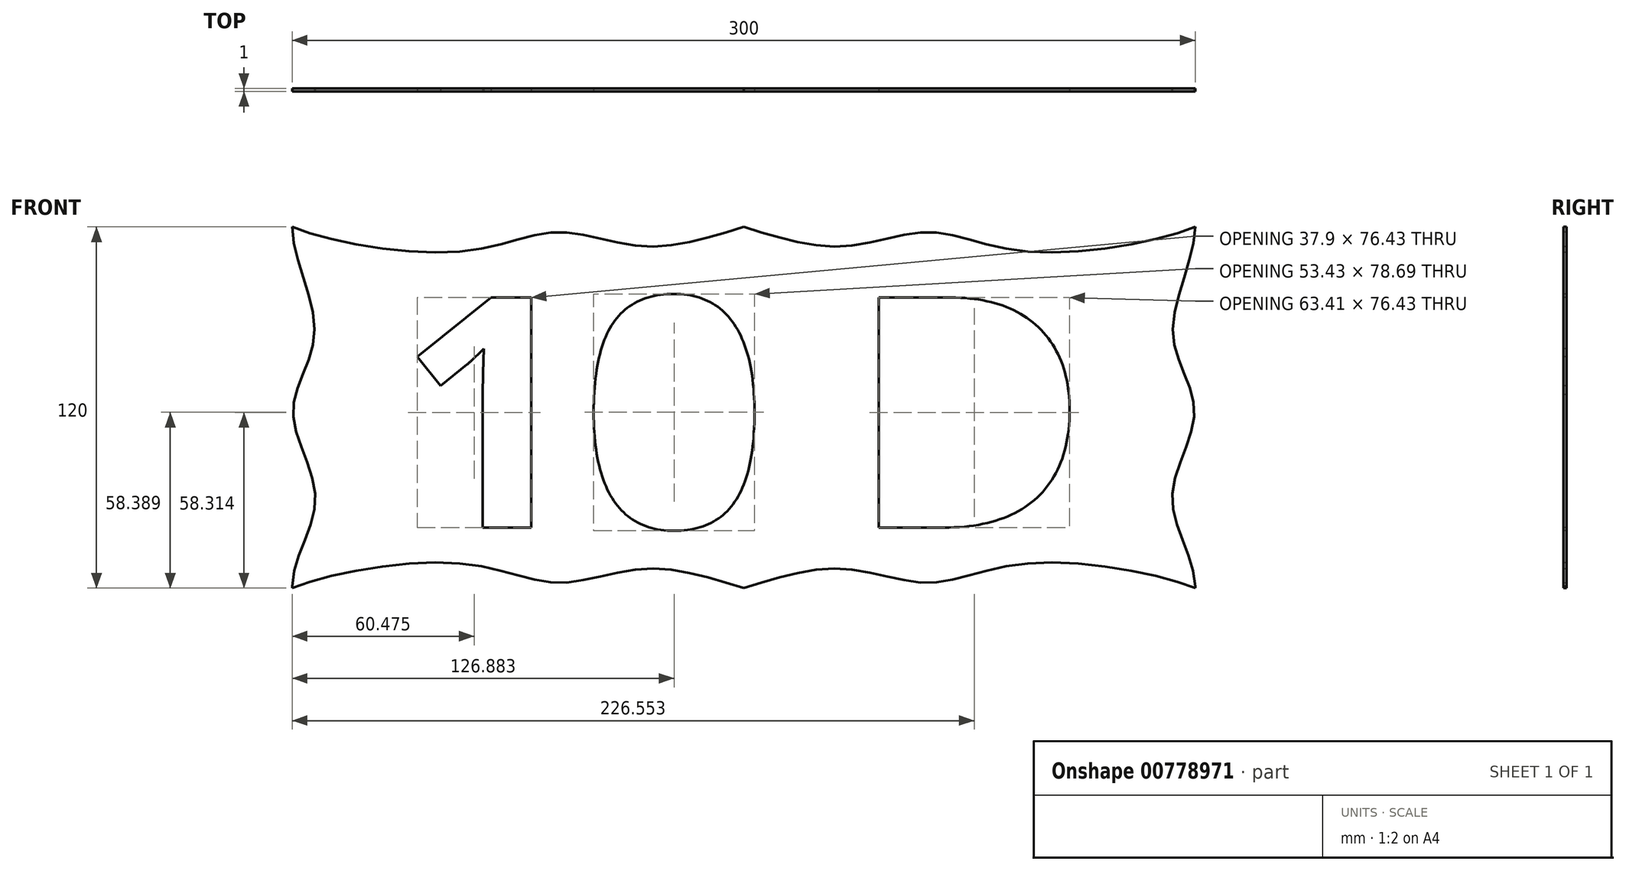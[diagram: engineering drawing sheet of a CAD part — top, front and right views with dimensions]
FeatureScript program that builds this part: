
annotation { "Feature Type Name" : "Feature", "Feature Type Description" : "" }
export const myFeature = defineFeature(function(context is Context, id is Id, definition is map)
    precondition{}
    {
        {
            var Q0;
            Q0=qCreatedBy(makeId("Front.planeOp"),FACE);
            var sketch = newSketch(context, id + "F0", { "sketchPlane" : qUnion([Q0])});
            skLineSegment(sketch, "E0.bottom", {"start": v(-150, 60) * mm, "end": v(150, 60) * mm});
            skLineSegment(sketch, "E0.top", {"start": v(-150, -60) * mm, "end": v(150, -60) * mm});
            skLineSegment(sketch, "E0.left", {"start": v(-150, 60) * mm, "end": v(-150, -60) * mm});
            skLineSegment(sketch, "E0.right", {"start": v(150, 60) * mm, "end": v(150, -60) * mm});
            skPoint(sketch, "E0.middle", {"position": v(0, 0) * mm});
            skSolve(sketch);
        }
        {
            var Q0;
            Q0 = qSketchRegion(id + "F0", true);
            extrude(context, id + "F1", {"entities" : qUnion([Q0]), "depth" : 1 * mm, "offsetDistance" : 25 * mm});
        }
        {
            var Q0;
            Q0=makeQuery(id+"F1.opExtrude","CAP_FACE",FACE,{"disambiguationData":[OSD([sQuery(id+"F0.wireOp",EDGE,"E0.bottom"),sQuery(id+"F0.wireOp",EDGE,"E0.top"),sQuery(id+"F0.wireOp",EDGE,"E0.left"),sQuery(id+"F0.wireOp",EDGE,"E0.right")])],"isStart":false});
            var sketch = newSketch(context, id + "F2", { "sketchPlane" : qUnion([Q0])});
            skText(sketch, "E1", { "text": "10 D", "fontName": "OpenSans-Bold.ttf"});
            const initialGuessF2  = {"E1": [-0.1148, -0.0399, 1, 0, 0.07708]};
            skSetInitialGuess(sketch, initialGuessF2);
            skSolve(sketch);
        }
        {
            var Q0;
            Q0 = qSketchRegion(id + "F2", true);
            extrude(context, id + "F3", {"entities" : qUnion([Q0]), "operationType" : NewBodyOperationType.REMOVE, "oppositeDirection" : true, "depth" : 1 * mm, "offsetDistance" : 25 * mm});
        }
        {
            var Q0;
            {var subQ0=sQuery(id+"F0.wireOp",EDGE,"E0.top");var subQ1=sQuery(id+"F0.wireOp",EDGE,"E0.right");var subQ2=sQuery(id+"F0.wireOp",EDGE,"E0.bottom");var subQ3=sQuery(id+"F0.wireOp",EDGE,"E0.left");Q0=makeQuery(id+"F3.boolean.opBoolean","SPLIT",FACE,{"disambiguationData":[TD([makeQuery(id+"F1.opExtrude","SWEPT_FACE",FACE,{"disambiguationData":[OSD([subQ2])]})])],"derivedFrom":makeQuery(id+"F1.opExtrude","CAP_FACE",FACE,{"disambiguationData":[OSD([subQ2,subQ0,subQ3,subQ1])],"isStart":false})});}
            var sketch = newSketch(context, id + "F4", { "sketchPlane" : qUnion([Q0])});
            skFitSpline(sketch, "E2", {"points": [v(0, 60) * mm, v(-32.64, 53.54) * mm, v(-61.53, 58.23) * mm, v(-93.56, 51.87) * mm, v(-150, 60) * mm], "startDerivative": vector(-134.57, -40.88) * mm, "endDerivative": vector(-118.6, 49.33) * mm});
            skFitSpline(sketch, "E3", {"points": [v(-150, 60) * mm, v(-142.55, 24.73) * mm, v(-149.7, -1.42) * mm, v(-142.31, -30.48) * mm, v(-150, -60) * mm], "startDerivative": vector(0.83, -120) * mm, "endDerivative": vector(1.63, -119.98) * mm});
            skFitSpline(sketch, "E4.MirrorCS", {"points": [v(0, -60) * mm, v(-32.64, -53.54) * mm, v(-61.53, -58.23) * mm, v(-93.56, -51.87) * mm, v(-150, -60) * mm], "startDerivative": vector(-134.57, 40.88) * mm, "endDerivative": vector(-118.6, -49.33) * mm});
            skFitSpline(sketch, "E5.MirrorCS", {"points": [v(0, -60) * mm, v(32.64, -53.54) * mm, v(61.53, -58.23) * mm, v(93.56, -51.87) * mm, v(150, -60) * mm], "startDerivative": vector(134.57, 40.88) * mm, "endDerivative": vector(118.6, -49.33) * mm});
            skFitSpline(sketch, "E6.MirrorCS", {"points": [v(0, 60) * mm, v(32.64, 53.54) * mm, v(61.53, 58.23) * mm, v(93.56, 51.87) * mm, v(150, 60) * mm], "startDerivative": vector(134.57, -40.88) * mm, "endDerivative": vector(118.6, 49.33) * mm});
            skFitSpline(sketch, "E7.MirrorCS", {"points": [v(150, 60) * mm, v(142.55, 24.73) * mm, v(149.7, -1.42) * mm, v(142.31, -30.48) * mm, v(150, -60) * mm], "startDerivative": vector(-0.83, -120) * mm, "endDerivative": vector(-1.63, -119.98) * mm});
            skSolve(sketch);
        }
        {
            var Q0;
            {var subQ3=sQuery(id+"F4.wireOp",EDGE,"E2");Q0=makeQuery(id+"F4.imprint","IMPRINT",FACE,{"disambiguationData":[TD([[makeQuery(id+"F4.imprint","IMPRINT",EDGE,{"derivedFrom":subQ3}),1.0]])]});}
            extrude(context, id + "F5", {"entities" : qUnion([Q0]), "operationType" : NewBodyOperationType.INTERSECT, "endBound" : BoundingType.THROUGH_ALL, "oppositeDirection" : true, "depth" : 1 * mm, "offsetDistance" : 25 * mm});
        }
    });
